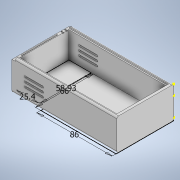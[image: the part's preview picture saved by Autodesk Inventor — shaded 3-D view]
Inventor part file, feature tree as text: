
AUTODESK INVENTOR PART (.ipt)
format: ipt  version: 2020.2 (Build 242310000, 310)  size: 297,984 bytes
history: native  units: mm
features: sketch x11, extrude x8, fillet x2, direct_edit x2, other x2, shell x1
ambient origin geometry x8: Origin, YZ Plane, XZ Plane, XY Plane, X Axis, Y Axis, Z Axis, Center Point
bodies: Solid1 (feature_tree)
feature tree (26):
  extrude  "Extrusion1"  Depth=3.0mm
  shell  "Shell1"  Thickness=25.0mm
  fillet  "Fillet1"  Radius=3.0mm
  sketch  "Sketch2"  dims[d11=2.0mm d12=10.0mm]
  direct_edit  "Direct Edit1"
  extrude  "Extrusion2"  Depth=10.0mm
  extrude  "Extrusion3"  Depth=1.5mm
  direct_edit  "Direct Edit2"
  sketch  "Sketch5"  dims[d17=118.5mm d18=0.0mm d19=10.0mm d20=0.0mm]
  extrude  "Extrusion6"  Depth=1.5mm
  extrude  "Extrusion7"  Depth=10.0mm TaperAngle=0.0deg
  extrude  "Extrusion8"  Depth=1.5mm
  extrude  "Extrusion9"  Depth=20.0mm
  fillet  "Fillet3"  Radius=1.25mm
  extrude  "Extrusion10"  Depth=3.0mm
  sketch  "Sketch15"  dims[d77=4.0mm d78=0.0mm]
  sketch  "Sketch17"  dims[d82=16.25mm d83=270.0deg d84=5.0mm d85=90.0deg d86=5.0mm d87=90.0deg d88=10.0mm d89=90.0deg d90=10.0mm d91=180.0deg d92=10.0mm d93=0.0mm d94=2.0mm d95=10.0mm d96=0.0mm d97=2.0mm d98=10.0mm d99=180.0deg d100=10.0mm d101=0.0mm d102=2.0mm d103=0.0mm d104=0.0mm d105=2.0mm d106=0.5mm d107=270.0deg d108=2.0mm d109=90.0deg d110=2.0mm d111=0.0mm d112=1.2mm d113=1.2mm d114=10.0mm d115=0.0mm d116=25.4mm d117=58.93mm d26=0.5mm d27=0.872665mm d28=0.5mm d29=0.872665mm d45=1.0mm d46=1.0mm d47=1.0mm d48=0.15mm d49=0.25mm d50=0.375mm d51=14.3117mm d52=0.75mm d53=20.594885mm d54=0.0625mm d55=0.75mm d56=0.375mm d66=1.0mm d67=1.0mm d68=1.0mm d69=0.15mm d70=0.25mm d71=0.375mm d72=14.3117mm d73=0.75mm d81=0.5mm d118=0.5mm d119=0.872665mm]
  sketch  "Sketch1"  dims[d6=86.0mm d7=66.0mm d8=25.0mm d9=0.0mm d10=3.0mm]
  sketch  "Sketch3"  dims[d13=2.0mm d14=1.5mm]
  sketch  "Sketch4"  dims[d15=1.5mm d16=1.5mm]
  sketch  "Sketch11"  dims[d21=1.0mm d22=1.5mm]
  sketch  "Sketch12"  dims[d23=33.5mm d24=20.0mm d25=1.25mm]
  sketch  "Sketch14"  dims[d74=1.0mm d75=-11.34464mm d76=3.0mm]
  sketch  "Sketch16"  dims[d79=4.0mm d80=0.0mm]
  other  "Size1"
  other  "Size2"
